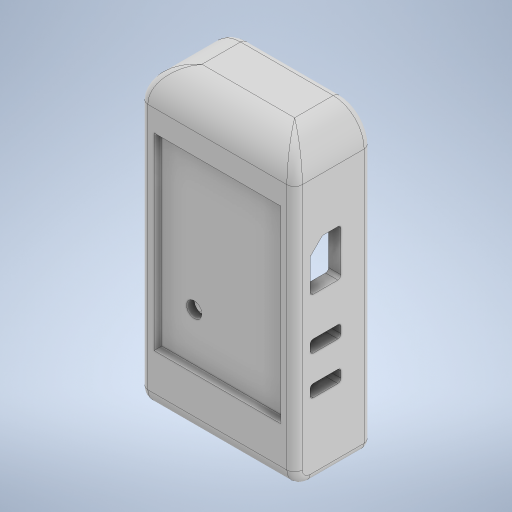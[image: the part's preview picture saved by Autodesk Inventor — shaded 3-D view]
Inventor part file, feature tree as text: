
AUTODESK INVENTOR PART (.ipt)
format: ipt  version: 2024 (Build 280153000, 153)  size: 542,208 bytes
history: native  units: mm
features: sketch x13, extrude x12, fillet x4, other x1
ambient origin geometry x8: Origin, YZ Plane, XZ Plane, XY Plane, X Axis, Y Axis, Z Axis, Center Point
bodies: Body1 (feature_tree)
feature tree (30):
  other  "Těleso1"
  extrude  "Vysunutí1"  Depth=100.0mm
  sketch  "Náčrt2"
  extrude  "Vysunutí3"  Depth=190.0mm
  fillet  "Zaoblení1"  Radius=50.0mm
  fillet  "Zaoblení2"  Radius=84.0mm
  extrude  "Vysunutí4"  Depth=110.0mm
  extrude  "Vysunutí5"  Depth=40.0mm TaperAngle=0.0deg
  extrude  "Vysunutí6"  Depth=20.0mm
  extrude  "Vysunutí8"  Depth=10.0mm
  fillet  "Zaoblení3"  Radius=20.0mm
  fillet  "Zaoblení4"  Radius=40.0mm
  extrude  "Vysunutí12"  Depth=5.0mm
  extrude  "Vysunutí13"  Depth=5.0mm
  extrude  "Vysunutí15"  Depth=5.0mm
  extrude  "Vysunutí16"  Depth=5.0mm
  extrude  "Vysunutí17"  Depth=10.0mm TaperAngle=0.0deg
  extrude  "Vysunutí18"  Depth=13.0mm
  sketch  "Náčrt1"
  sketch  "Náčrt4"
  sketch  "Náčrt5"
  sketch  "Náčrt6"
  sketch  "Náčrt9"
  sketch  "Náčrt11"
  sketch  "Náčrt17"
  sketch  "Náčrt18"
  sketch  "Náčrt20"
  sketch  "Náčrt21"
  sketch  "Náčrt25"
  sketch  "Náčrt26"
